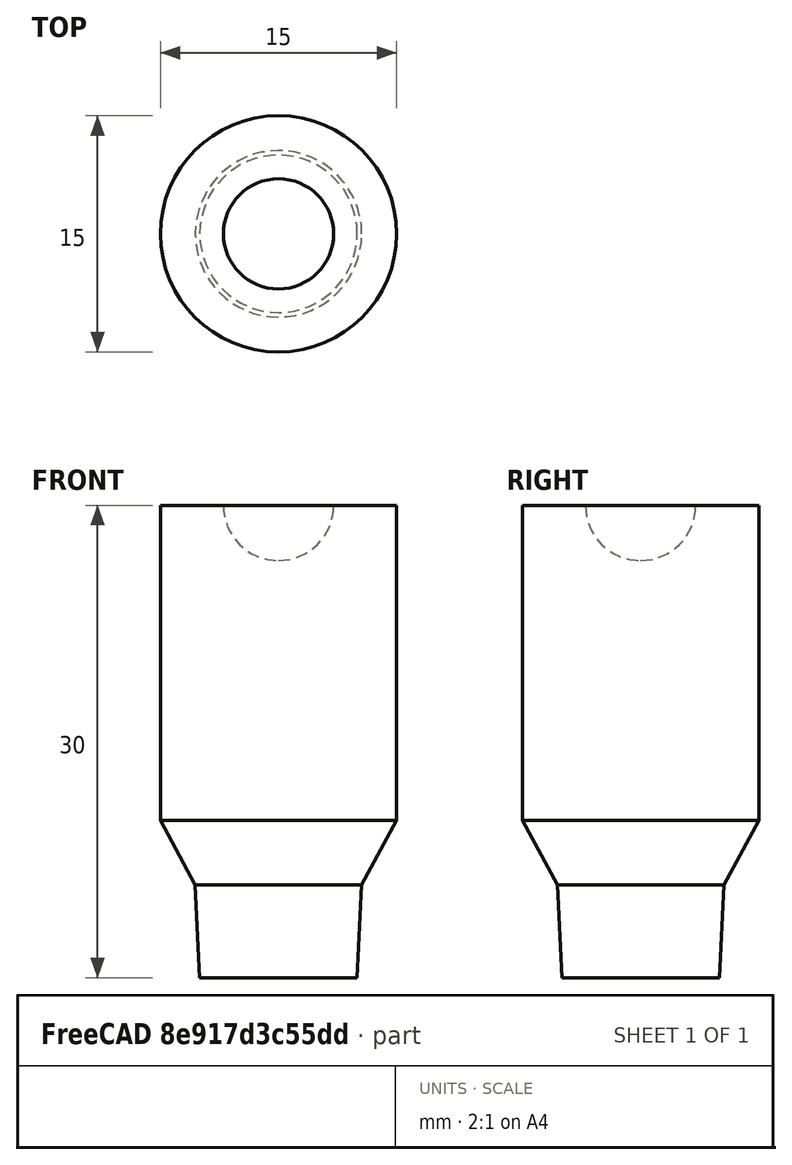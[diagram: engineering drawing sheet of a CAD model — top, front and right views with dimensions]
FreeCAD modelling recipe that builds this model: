
FCSTD DOCUMENT  (FreeCAD 0.16R6712 (Git))
Label: zylinder
License: All rights reserved
LicenseURL: http://en.wikipedia.org/wiki/All_rights_reserved
objects: Sketcher::SketchObject×1, PartDesign::Revolution×1
note: 3 computed .brp shape members not serialized (recipe doc carries the construction recipe); baked Part::Feature solids carry a one-line shape summary decoded from their .brp

FEATURE [Sketcher::SketchObject] Sketch
  Placement = pos=(0,0,0) rot=(-1,0,0;4.71239rad)
  sketch-geometry (7):
    g0: LineSegment StartX=0 StartY=0 StartZ=0 EndX=-5 EndY=0 EndZ=0
    g1: LineSegment StartX=-7.5 StartY=10 StartZ=0 EndX=-7.5 EndY=30 EndZ=0
    g2: ArcOfCircle CenterX=0 CenterY=30 CenterZ=0 NormalX=0 NormalY=0 NormalZ=1 Radius=3.5 StartAngle=3.14159 EndAngle=4.71239
    g3: LineSegment StartX=-7.5 StartY=30 StartZ=0 EndX=-3.5 EndY=30 EndZ=0
    g4: LineSegment StartX=0 StartY=26.5 StartZ=0 EndX=0 EndY=0 EndZ=0
    g5: LineSegment StartX=-5 StartY=0 StartZ=0 EndX=-5.28672 EndY=5.90375 EndZ=0
    g6: LineSegment StartX=-5.28672 StartY=5.90375 StartZ=0 EndX=-7.5 EndY=10 EndZ=0
  constraints (20):
    c: Coincident(g-1,g0)
    c: Horizontal(g0)
    c: Vertical(g1)
    c: DistanceX(g0,g0) = 5
    c: DistanceY(g-1,g1) = 10
    c: DistanceY(g-1,g1) = 30
    c: PointOnObject(g2,g-2)
    c: Coincident(g3,g1)
    c: Coincident(g3,g2)
    c: Horizontal(g3)
    c: PointOnObject(g2,g-2)
    c: DistanceX(g2,g-1) = 3.5
    c: PointOnObject(g2,g3)
    c: Coincident(g4,g2)
    c: Vertical(g4)
    c: Coincident(g-1,g4)
    c: Coincident(g5,g0)
    c: Coincident(g6,g5)
    c: Coincident(g6,g1)
    c: DistanceX(g1,g-1) = 7.5
FEATURE [PartDesign::Revolution] Revolution
  Angle = 360
  Axis = (0,0,1)
  Base = (0,0,0)
  Placement = pos=(0,0,0) rot=(-1,0,0;4.71239rad)
  ReferenceAxis = -> Sketch [V_Axis]
  Sketch = -> Sketch
